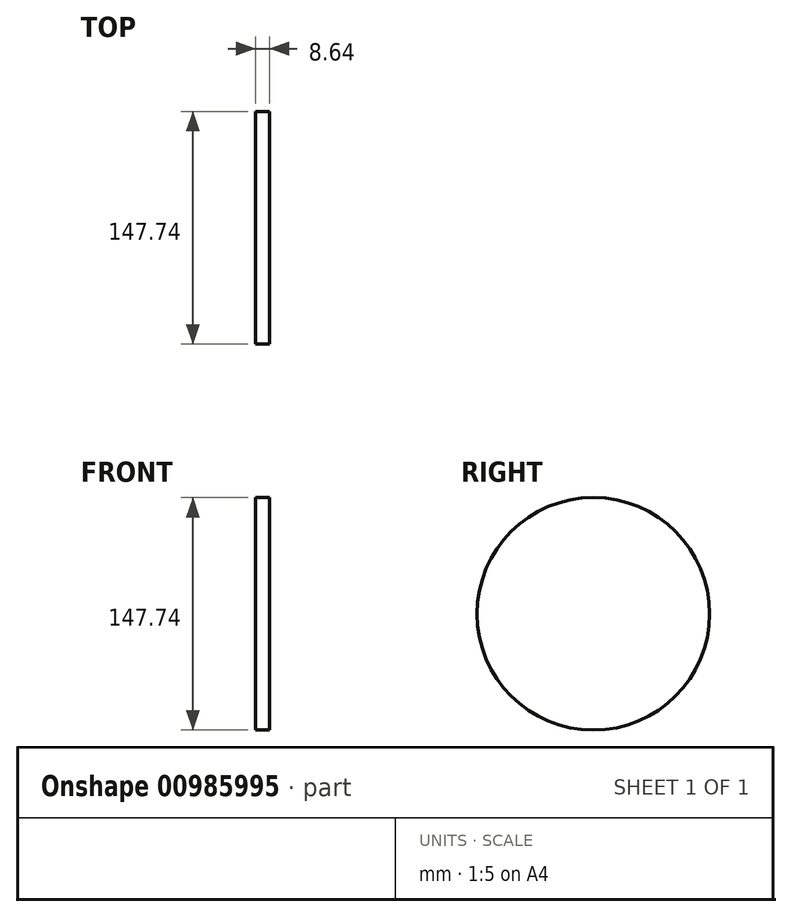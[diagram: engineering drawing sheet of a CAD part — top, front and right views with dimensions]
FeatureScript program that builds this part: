
annotation { "Feature Type Name" : "Feature", "Feature Type Description" : "" }
export const myFeature = defineFeature(function(context is Context, id is Id, definition is map)
    precondition{}
    {
        {
            var Q0;
            Q0=qCreatedBy(makeId("Right.planeOp"),FACE);
            var sketch = newSketch(context, id + "F0", { "sketchPlane" : qUnion([Q0])});
            skCircle(sketch, "E0", {"center": v(0, 0) * mm, "radius": 73.87 * mm});
            skCircle(sketch, "E1", {"center": v(-5.19, 9.82) * mm, "radius": 18.93 * mm});
            skSolve(sketch);
        }
        {
            var Q0;
            Q0=makeQuery(id+"F0.imprint","IMPRINT",FACE,{"disambiguationData":[TD([[makeQuery(id+"F0.imprint","IMPRINT",EDGE,{"derivedFrom":sQuery(id+"F0.wireOp",EDGE,"E1")}),1.0]])]});
            var Q1;
            Q1=makeQuery(id+"F0.imprint","IMPRINT",FACE,{"disambiguationData":[TD([[makeQuery(id+"F0.imprint","IMPRINT",EDGE,{"derivedFrom":sQuery(id+"F0.wireOp",EDGE,"E0")}),1.0]])]});
            extrude(context, id + "F1", {"entities" : qUnion([Q0, Q1]), "depth" : 8.64 * mm, "offsetDistance" : 25.4 * mm});
        }
    });
